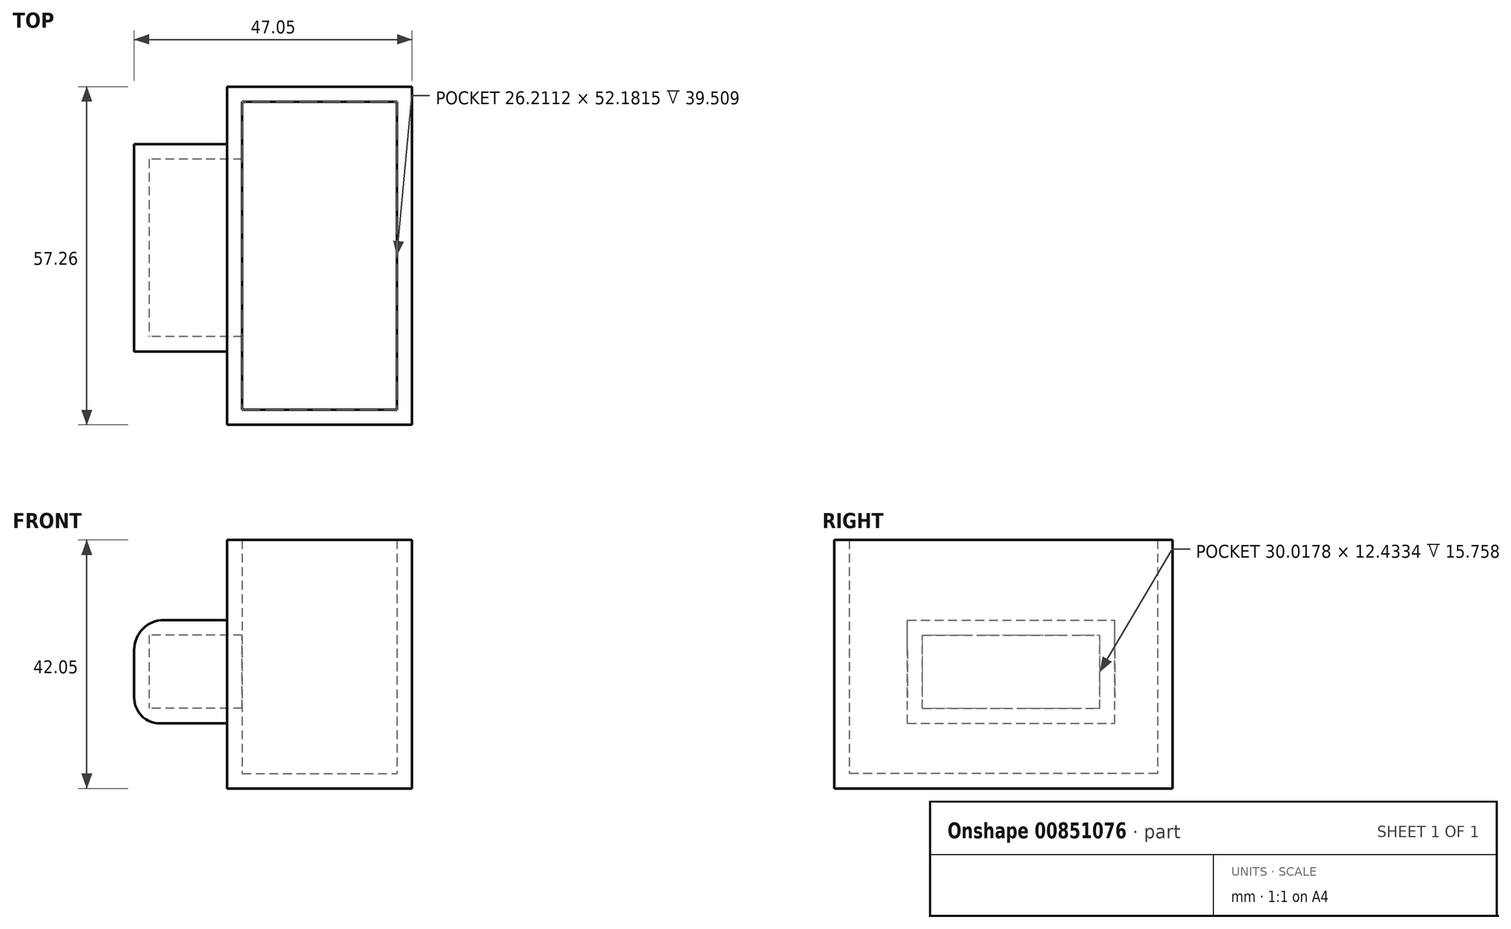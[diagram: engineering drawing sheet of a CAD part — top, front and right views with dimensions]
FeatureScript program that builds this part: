
annotation { "Feature Type Name" : "Feature", "Feature Type Description" : "" }
export const myFeature = defineFeature(function(context is Context, id is Id, definition is map)
    precondition{}
    {
        {
            var Q0;
            Q0=qCreatedBy(makeId("Top.planeOp"),FACE);
            var sketch = newSketch(context, id + "F0", { "sketchPlane" : qUnion([Q0])});
            skLineSegment(sketch, "E0.bottom", {"start": v(15.76, 66.89) * mm, "end": v(47.05, 66.89) * mm});
            skLineSegment(sketch, "E0.top", {"start": v(15.76, 9.63) * mm, "end": v(47.05, 9.63) * mm});
            skLineSegment(sketch, "E0.left", {"start": v(15.76, 66.89) * mm, "end": v(15.76, 9.63) * mm});
            skLineSegment(sketch, "E0.right", {"start": v(47.05, 66.89) * mm, "end": v(47.05, 9.63) * mm});
            skSolve(sketch);
        }
        {
            var Q0;
            Q0=makeQuery(id+"F0.imprint","IMPRINT",FACE,{"disambiguationData":[TD([[makeQuery(id+"F0.imprint","IMPRINT",EDGE,{"derivedFrom":sQuery(id+"F0.wireOp",EDGE,"E0.bottom")}),-1.0]])]});
            extrude(context, id + "F1", {"entities" : qUnion([Q0]), "depth" : 42.05 * mm, "offsetDistance" : 25.4 * mm});
        }
        {
            var Q0;
            Q0=qCreatedBy(makeId("Right.planeOp"),FACE);
            var sketch = newSketch(context, id + "F2", { "sketchPlane" : qUnion([Q0])});
            skLineSegment(sketch, "E1.bottom", {"start": v(57.13, 28.51) * mm, "end": v(22.04, 28.51) * mm});
            skLineSegment(sketch, "E1.top", {"start": v(57.13, 11) * mm, "end": v(22.04, 11) * mm});
            skLineSegment(sketch, "E1.left", {"start": v(57.13, 28.51) * mm, "end": v(57.13, 11) * mm});
            skLineSegment(sketch, "E1.right", {"start": v(22.04, 28.51) * mm, "end": v(22.04, 11) * mm});
            skSolve(sketch);
        }
        {
            var Q0;
            Q0 = qSketchRegion(id + "F2", true);
            extrude(context, id + "F3", {"entities" : qUnion([Q0]), "operationType" : NewBodyOperationType.ADD, "depth" : 25.4 * mm, "offsetDistance" : 25.4 * mm});
        }
        {
            var Q0;
            Q0=makeQuery(id+"F1.opExtrude","CAP_FACE",FACE,{"disambiguationData":[OSD([sQuery(id+"F0.wireOp",EDGE,"E0.bottom"),sQuery(id+"F0.wireOp",EDGE,"E0.top"),sQuery(id+"F0.wireOp",EDGE,"E0.left"),sQuery(id+"F0.wireOp",EDGE,"E0.right")])],"isStart":false});
            shell(context, id + "F4", {"entities" : qUnion([Q0]), "thickness" : 2.54 * mm});
        }
        {
            var Q0;
            Q0=makeQuery(id+"F3.opExtrude","CAP_EDGE",EDGE,{"disambiguationData":[OSD([sQuery(id+"F2.wireOp",EDGE,"E1.top")])],"isStart":true});
            fillet(context, id + "F5", {"entities" : qUnion([Q0]), "radius" : 4.36 * mm, "tangentPropagation" : true, "allowEdgeOverflow" : false});
        }
        {
            var Q0;
            Q0=makeQuery(id+"F3.opExtrude","CAP_EDGE",EDGE,{"disambiguationData":[OSD([sQuery(id+"F2.wireOp",EDGE,"E1.bottom")])],"isStart":true});
            fillet(context, id + "F6", {"entities" : qUnion([Q0]), "radius" : 5.08 * mm, "tangentPropagation" : true, "allowEdgeOverflow" : false});
        }
    });
